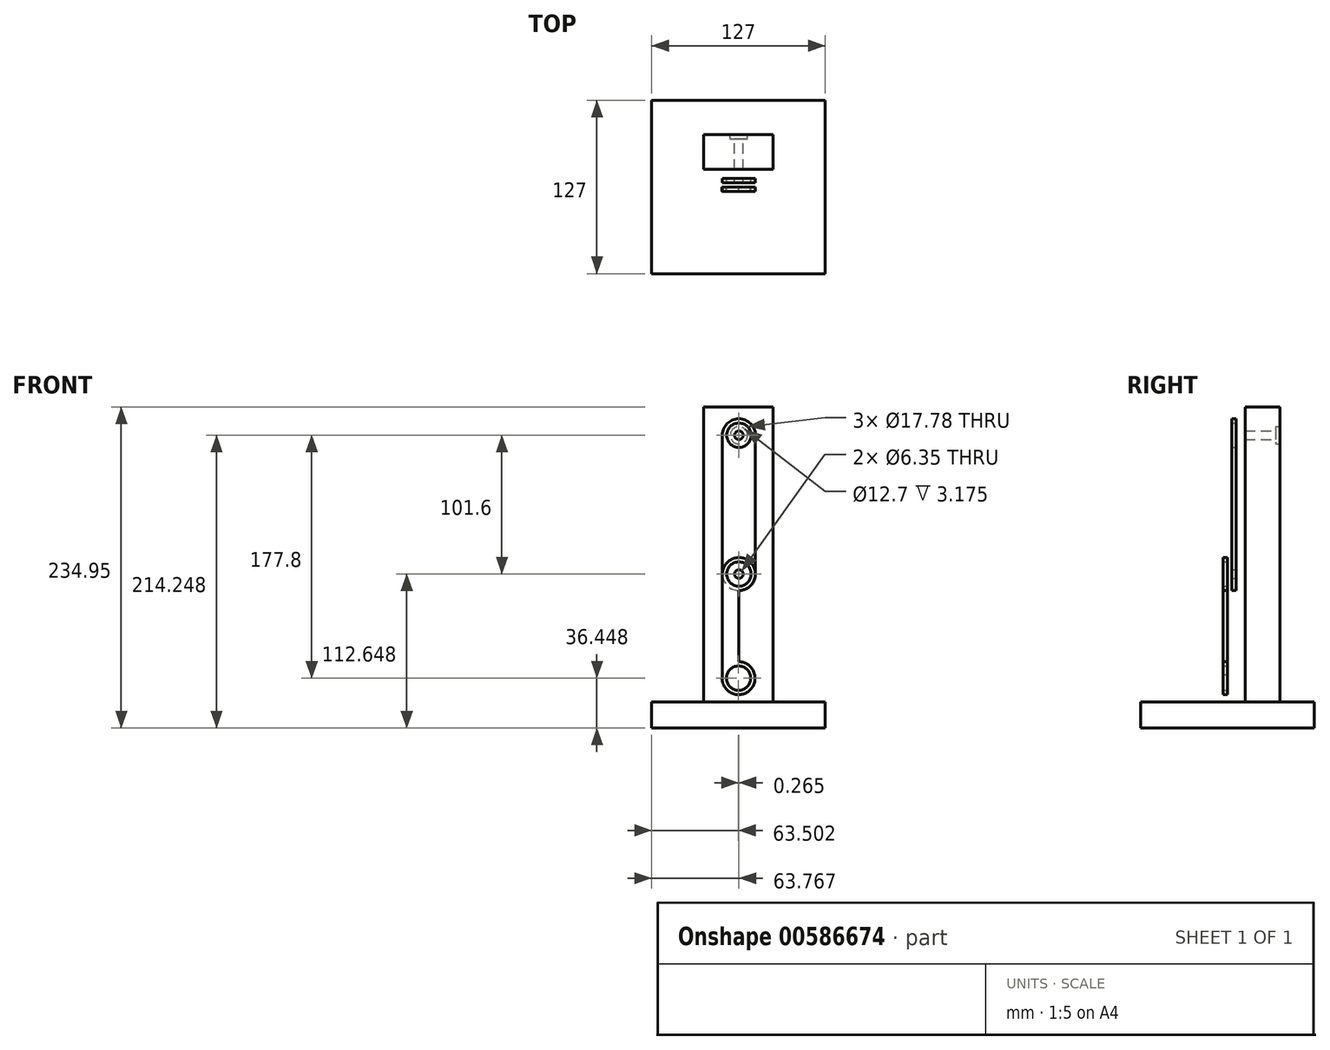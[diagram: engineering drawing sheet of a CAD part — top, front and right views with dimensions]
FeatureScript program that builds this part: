
annotation { "Feature Type Name" : "Feature", "Feature Type Description" : "" }
export const myFeature = defineFeature(function(context is Context, id is Id, definition is map)
    precondition{}
    {
        {
            var Q0;
            Q0=qCreatedBy(makeId("Front.planeOp"),FACE);
            var sketch = newSketch(context, id + "F0", { "sketchPlane" : qUnion([Q0])});
            skCircle(sketch, "E0", {"center": v(-48.95, 80.9) * mm, "radius": 8.9 * mm});
            skCircle(sketch, "E1.0", {"center": v(-48.95, 80.9) * mm, "radius": 12.07 * mm});
            skCircle(sketch, "E2.0", {"center": v(-48.95, -20.7) * mm, "radius": 12.07 * mm});
            skLineSegment(sketch, "E3", {"start": v(-61.02, 80.9) * mm, "end": v(-61.02, -20.7) * mm});
            skLineSegment(sketch, "E4", {"start": v(-36.89, -20.7) * mm, "end": v(-36.89, 80.9) * mm});
            skCircle(sketch, "E5", {"center": v(-48.95, -20.7) * mm, "radius": 3.18 * mm});
            skSolve(sketch);
        }
        {
            var Q0;
            Q0=makeQuery(id+"F0.imprint","IMPRINT",FACE,{"disambiguationData":[TD([[makeQuery(id+"F0.imprint","IMPRINT",EDGE,{"derivedFrom":sQuery(id+"F0.wireOp",EDGE,"E0")}),-1.0]])]});
            var Q1;
            {var subQ0=sQuery(id+"F0.wireOp",EDGE,"E3");Q1=makeQuery(id+"F0.imprint","IMPRINT",FACE,{"disambiguationData":[TD([[makeQuery(id+"F0.imprint","IMPRINT",EDGE,{"derivedFrom":subQ0}),1.0]])]});}
            var Q2;
            Q2=makeQuery(id+"F0.imprint","IMPRINT",FACE,{"disambiguationData":[TD([[makeQuery(id+"F0.imprint","IMPRINT",EDGE,{"derivedFrom":sQuery(id+"F0.wireOp",EDGE,"E5")}),-1.0]])]});
            extrude(context, id + "F1", {"entities" : qUnion([Q0, Q1, Q2]), "depth" : 3.17 * mm, "offsetDistance" : 25.4 * mm});
        }
        {
            var Q0;
            Q0=qCreatedBy(makeId("Front.planeOp"),FACE);
            cPlane(context, id + "F2", {"entities" : qUnion([Q0]), "cplaneType" : CPlaneType.OFFSET, "offset" : 6.35 * mm, "width" : 152.4 * mm, "height" : 152.4 * mm});
        }
        {
            var Q0;
            Q0=qCreatedBy(id+"F2.planeOp",FACE);
            var sketch = newSketch(context, id + "F3", { "sketchPlane" : qUnion([Q0])});
            skCircle(sketch, "E6.0", {"center": v(-48.95, -20.7) * mm, "radius": 3.18 * mm});
            skCircle(sketch, "E7", {"center": v(-48.95, -20.7) * mm, "radius": 8.9 * mm});
            skCircle(sketch, "E8", {"center": v(-49.22, -96.9) * mm, "radius": 8.9 * mm});
            skCircle(sketch, "E9.0", {"center": v(-48.95, -20.7) * mm, "radius": 12.07 * mm});
            skCircle(sketch, "E10.0", {"center": v(-49.22, -96.9) * mm, "radius": 12.07 * mm});
            skLineSegment(sketch, "E11", {"start": v(-61.02, -20.7) * mm, "end": v(-61.02, -96.9) * mm});
            skLineSegment(sketch, "E12", {"start": v(-37.15, -96.9) * mm, "end": v(-37.15, -20.7) * mm});
            skLineSegment(sketch, "E13", {"start": v(-49, -8.64) * mm, "end": v(-49, -108.96) * mm});
            skSolve(sketch);
        }
        {
            var Q0;
            {var subQ0=sQuery(id+"F3.wireOp",EDGE,"E11");var subQ1=sQuery(id+"F3.wireOp",EDGE,"E9.0");var subQ2=makeQuery(id+"F3.imprint","INTERSECT",VERTEX,{"derivedFrom":[subQ1,subQ0]});Q0=makeQuery(id+"F3.imprint","IMPRINT",FACE,{"disambiguationData":[TD([[makeQuery(id+"F3.imprint","IMPRINT",EDGE,{"disambiguationData":[TD([[subQ2,-1.0]])],"derivedFrom":subQ1}),-1.0]])]});}
            var Q1;
            Q1=makeQuery(id+"F3.imprint","IMPRINT",FACE,{"disambiguationData":[TD([[makeQuery(id+"F3.imprint","IMPRINT",EDGE,{"derivedFrom":sQuery(id+"F3.wireOp",EDGE,"E7")}),-1.0]])]});
            var Q2;
            Q2=makeQuery(id+"F3.imprint","IMPRINT",FACE,{"disambiguationData":[TD([[makeQuery(id+"F3.imprint","IMPRINT",EDGE,{"derivedFrom":sQuery(id+"F3.wireOp",EDGE,"E8")}),-1.0]])]});
            extrude(context, id + "F4", {"entities" : qUnion([Q0, Q1, Q2]), "depth" : 3.17 * mm, "offsetDistance" : 25.4 * mm});
        }
        {
            var Q0;
            Q0=qCreatedBy(makeId("Top.planeOp"),FACE);
            cPlane(context, id + "F5", {"entities" : qUnion([Q0]), "cplaneType" : CPlaneType.OFFSET, "offset" : 114.3 * mm, "oppositeDirection" : true, "width" : 152.4 * mm, "height" : 152.4 * mm});
        }
        {
            var Q0;
            Q0=qCreatedBy(id+"F5.planeOp",FACE);
            var sketch = newSketch(context, id + "F6", { "sketchPlane" : qUnion([Q0])});
            skLineSegment(sketch, "E14.0", {"start": v(-40.33, -6.35) * mm, "end": v(-58.1, -6.35) * mm});
            skLineSegment(sketch, "E15", {"start": v(-49.22, -6.35) * mm, "end": v(-49.22, 57.15) * mm});
            skPoint(sketch, "E15.endSnap0", {"position": v(-49.22, -6.35) * mm});
            skLineSegment(sketch, "E16", {"start": v(14.28, 57.15) * mm, "end": v(14.28, -69.85) * mm});
            skLineSegment(sketch, "E17", {"start": v(14.28, -69.85) * mm, "end": v(-112.72, -69.85) * mm});
            skLineSegment(sketch, "E18", {"start": v(-112.72, -69.85) * mm, "end": v(-112.72, 57.15) * mm});
            skLineSegment(sketch, "E19", {"start": v(-112.72, 57.15) * mm, "end": v(-49.22, 57.15) * mm});
            skLineSegment(sketch, "E20", {"start": v(-49.22, 57.15) * mm, "end": v(14.28, 57.15) * mm});
            skSolve(sketch);
        }
        {
            var Q0;
            Q0=makeQuery(id+"F6.imprint","IMPRINT",FACE,{"disambiguationData":[TD([[makeQuery(id+"F6.imprint","IMPRINT",EDGE,{"derivedFrom":sQuery(id+"F6.wireOp",EDGE,"E16")}),-1.0]])]});
            extrude(context, id + "F7", {"entities" : qUnion([Q0]), "oppositeDirection" : true, "depth" : 19.05 * mm, "offsetDistance" : 25.4 * mm});
        }
        {
            var Q0;
            Q0=qCreatedBy(id+"F5.planeOp",FACE);
            var sketch = newSketch(context, id + "F8", { "sketchPlane" : qUnion([Q0])});
            skLineSegment(sketch, "E21.0", {"start": v(-40.33, -6.35) * mm, "end": v(-58.1, -6.35) * mm});
            skLineSegment(sketch, "E22", {"start": v(-49.22, 6.57) * mm, "end": v(-23.82, 6.57) * mm});
            skPoint(sketch, "E22.startSnap0", {"position": v(-49.22, -6.35) * mm});
            skLineSegment(sketch, "E23", {"start": v(-23.82, 6.57) * mm, "end": v(-23.82, 31.97) * mm});
            skLineSegment(sketch, "E24", {"start": v(-23.82, 31.97) * mm, "end": v(-74.62, 31.97) * mm});
            skLineSegment(sketch, "E25", {"start": v(-74.62, 31.97) * mm, "end": v(-74.62, 6.57) * mm});
            skLineSegment(sketch, "E26", {"start": v(-74.62, 6.57) * mm, "end": v(-49.22, 6.57) * mm});
            skSolve(sketch);
        }
        {
            var Q0;
            Q0=makeQuery(id+"F8.imprint","IMPRINT",FACE,{"disambiguationData":[TD([[makeQuery(id+"F8.imprint","IMPRINT",EDGE,{"derivedFrom":sQuery(id+"F8.wireOp",EDGE,"E22")}),1.0]])]});
            extrude(context, id + "F9", {"entities" : qUnion([Q0]), "operationType" : NewBodyOperationType.ADD, "depth" : 215.9 * mm, "offsetDistance" : 25.4 * mm});
        }
        {
            var Q0;
            Q0=makeQuery(id+"F9.opExtrude","SWEPT_FACE",FACE,{"disambiguationData":[OSD([sQuery(id+"F8.wireOp",EDGE,"E24")])]});
            var sketch = newSketch(context, id + "F10", { "sketchPlane" : qUnion([Q0])});
            skCircle(sketch, "E27", {"center": v(48.95, 80.9) * mm, "radius": 3.18 * mm});
            skCircle(sketch, "E28", {"center": v(48.95, 80.9) * mm, "radius": 6.35 * mm});
            skSolve(sketch);
        }
        {
            var Q0;
            Q0=makeQuery(id+"F10.imprint","IMPRINT",FACE,{"disambiguationData":[TD([[makeQuery(id+"F10.imprint","IMPRINT",EDGE,{"derivedFrom":sQuery(id+"F10.wireOp",EDGE,"E27")}),1.0]])]});
            extrude(context, id + "F11", {"entities" : qUnion([Q0]), "operationType" : NewBodyOperationType.REMOVE, "endBound" : BoundingType.THROUGH_ALL, "oppositeDirection" : true, "depth" : 25.4 * mm, "offsetDistance" : 25.4 * mm});
        }
        {
            var Q0;
            Q0=makeQuery(id+"F10.imprint","IMPRINT",FACE,{"disambiguationData":[TD([[makeQuery(id+"F10.imprint","IMPRINT",EDGE,{"derivedFrom":sQuery(id+"F10.wireOp",EDGE,"E27")}),-1.0]])]});
            var Q1;
            Q1=makeQuery(id+"F10.imprint","IMPRINT",FACE,{"disambiguationData":[TD([[makeQuery(id+"F10.imprint","IMPRINT",EDGE,{"derivedFrom":sQuery(id+"F10.wireOp",EDGE,"E27")}),1.0]])]});
            extrude(context, id + "F12", {"entities" : qUnion([Q0, Q1]), "operationType" : NewBodyOperationType.REMOVE, "oppositeDirection" : true, "depth" : 3.17 * mm, "offsetDistance" : 25.4 * mm});
        }
    });
